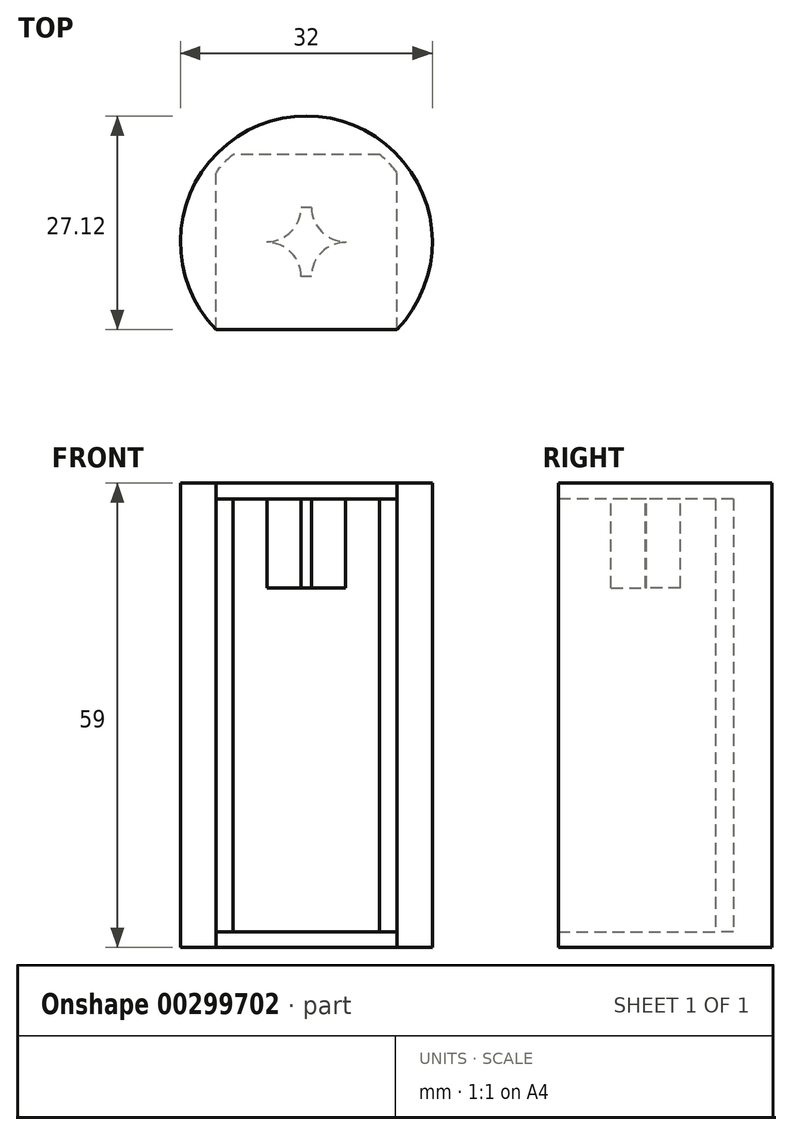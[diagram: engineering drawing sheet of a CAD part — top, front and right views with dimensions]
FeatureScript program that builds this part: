
annotation { "Feature Type Name" : "Feature", "Feature Type Description" : "" }
export const myFeature = defineFeature(function(context is Context, id is Id, definition is map)
    precondition{}
    {
        {
            var Q0;
            Q0=qCreatedBy(makeId("Top.planeOp"),FACE);
            var sketch = newSketch(context, id + "F0", { "sketchPlane" : qUnion([Q0])});
            skCircle(sketch, "E0", {"center": v(0, 0) * mm, "radius": 16 * mm});
            skCircle(sketch, "E1", {"center": v(0, 0) * mm, "radius": 14.5 * mm});
            skSolve(sketch);
        }
        {
            var Q0;
            Q0 = qSketchRegion(id + "F0", true);
            extrude(context, id + "F1", {"entities" : qUnion([Q0]), "depth" : 55 * mm});
        }
        {
            var Q0;
            Q0=makeQuery(id+"F1.opExtrude","CAP_FACE",FACE,{"disambiguationData":[OSD([sQuery(id+"F0.wireOp",EDGE,"E0"),sQuery(id+"F0.wireOp",EDGE,"E1")])],"isStart":false});
            var sketch = newSketch(context, id + "F2", { "sketchPlane" : qUnion([Q0])});
            skCircle(sketch, "E2", {"center": v(0, 0) * mm, "radius": 16 * mm});
            skSolve(sketch);
        }
        {
            var Q0;
            Q0 = qSketchRegion(id + "F2", true);
            extrude(context, id + "F3", {"entities" : qUnion([Q0]), "operationType" : NewBodyOperationType.ADD, "depth" : 2 * mm});
        }
        {
            var Q0;
            Q0=makeQuery(id+"F1.opExtrude","CAP_FACE",FACE,{"disambiguationData":[OSD([sQuery(id+"F0.wireOp",EDGE,"E0"),sQuery(id+"F0.wireOp",EDGE,"E1")])],"isStart":true});
            var sketch = newSketch(context, id + "F4", { "sketchPlane" : qUnion([Q0])});
            skCircle(sketch, "E3", {"center": v(0, 0) * mm, "radius": 16 * mm});
            skSolve(sketch);
        }
        {
            var Q0;
            Q0 = qSketchRegion(id + "F4", true);
            extrude(context, id + "F5", {"entities" : qUnion([Q0]), "operationType" : NewBodyOperationType.ADD, "depth" : 2 * mm});
        }
        {
            var Q0;
            Q0=makeQuery(id+"F5.opExtrude","CAP_FACE",FACE,{"disambiguationData":[OSD([sQuery(id+"F4.wireOp",EDGE,"E3")])],"isStart":false});
            var sketch = newSketch(context, id + "F6", { "sketchPlane" : qUnion([Q0])});
            skLineSegment(sketch, "E4.bottom", {"start": v(11.5, -11.12) * mm, "end": v(-11.5, -11.12) * mm});
            skLineSegment(sketch, "E4.top", {"start": v(11.5, 11.12) * mm, "end": v(-11.5, 11.12) * mm});
            skLineSegment(sketch, "E4.left", {"start": v(11.5, -11.12) * mm, "end": v(11.5, 11.12) * mm});
            skLineSegment(sketch, "E4.right", {"start": v(-11.5, -11.12) * mm, "end": v(-11.5, 11.12) * mm});
            skPoint(sketch, "E4.middle", {"position": v(0, 0) * mm});
            skSolve(sketch);
        }
        {
            var Q0;
            {var subQ0=sQuery(id+"F6.wireOp",EDGE,"E4.top");Q0=makeQuery(id+"F6.imprint","IMPRINT",FACE,{"disambiguationData":[TD([[makeQuery(id+"F6.imprint","IMPRINT",EDGE,{"derivedFrom":subQ0}),-1.0]])]});}
            extrude(context, id + "F7", {"entities" : qUnion([Q0]), "operationType" : NewBodyOperationType.REMOVE, "endBound" : BoundingType.THROUGH_ALL, "oppositeDirection" : true, "depth" : 25 * mm});
        }
        {
            var Q0;
            Q0=makeQuery(id+"F5.opExtrude","CAP_FACE",FACE,{"disambiguationData":[OSD([sQuery(id+"F4.wireOp",EDGE,"E3")])],"isStart":false});
            var sketch = newSketch(context, id + "F8", { "sketchPlane" : qUnion([Q0])});
            skLineSegment(sketch, "E5.bottom", {"start": v(11.5, 11.12) * mm, "end": v(-11.5, 11.12) * mm});
            skLineSegment(sketch, "E5.top", {"start": v(11.5, -11.12) * mm, "end": v(-11.5, -11.12) * mm});
            skLineSegment(sketch, "E5.left", {"start": v(11.5, 11.12) * mm, "end": v(11.5, -11.12) * mm});
            skLineSegment(sketch, "E5.right", {"start": v(-11.5, 11.12) * mm, "end": v(-11.5, -11.12) * mm});
            skPoint(sketch, "E5.middle", {"position": v(0, 0) * mm});
            skSolve(sketch);
        }
        {
            var Q0;
            {var subQ0=sQuery(id+"F8.wireOp",EDGE,"E5.right");Q0=makeQuery(id+"F8.imprint","IMPRINT",FACE,{"disambiguationData":[TD([[makeQuery(id+"F8.imprint","IMPRINT",EDGE,{"derivedFrom":subQ0}),-1.0]])]});}
            var Q1;
            {var subQ0=sQuery(id+"F8.wireOp",EDGE,"E5.top");Q1=makeQuery(id+"F8.imprint","IMPRINT",FACE,{"disambiguationData":[TD([[makeQuery(id+"F8.imprint","IMPRINT",EDGE,{"derivedFrom":subQ0}),1.0]])]});}
            var Q2;
            {var subQ0=sQuery(id+"F8.wireOp",EDGE,"E5.left");Q2=makeQuery(id+"F8.imprint","IMPRINT",FACE,{"disambiguationData":[TD([[makeQuery(id+"F8.imprint","IMPRINT",EDGE,{"derivedFrom":subQ0}),1.0]])]});}
            extrude(context, id + "F9", {"entities" : qUnion([Q0, Q1, Q2]), "operationType" : NewBodyOperationType.ADD, "oppositeDirection" : true, "depth" : 58 * mm});
        }
        {
            var Q0;
            Q0=makeQuery(id+"F7.boolean.opBoolean","COPY",FACE,{"derivedFrom":makeQuery(id+"F7.opExtrude","SWEPT_FACE",FACE,{"disambiguationData":[OSD([sQuery(id+"F6.wireOp",EDGE,"E4.top")])]})});
            var sketch = newSketch(context, id + "F10", { "sketchPlane" : qUnion([Q0])});
            skLineSegment(sketch, "E6.bottom", {"start": v(-11.5, 0) * mm, "end": v(11.5, 0) * mm});
            skLineSegment(sketch, "E6.top", {"start": v(-11.5, 55) * mm, "end": v(11.5, 55) * mm});
            skLineSegment(sketch, "E6.left", {"start": v(-11.5, 0) * mm, "end": v(-11.5, 55) * mm});
            skLineSegment(sketch, "E6.right", {"start": v(11.5, 0) * mm, "end": v(11.5, 55) * mm});
            skSolve(sketch);
        }
        {
            var Q0;
            Q0 = qSketchRegion(id + "F10", true);
            extrude(context, id + "F11", {"entities" : qUnion([Q0]), "operationType" : NewBodyOperationType.REMOVE, "oppositeDirection" : true, "depth" : 3 * mm});
        }
        {
            var Q0;
            Q0=makeQuery(id+"F11.boolean.opBoolean","MERGE",FACE,{"derivedFrom":[makeQuery(id+"F3.opExtrude","CAP_FACE",FACE,{"disambiguationData":[OSD([sQuery(id+"F2.wireOp",EDGE,"E2")])],"isStart":true}),makeQuery(id+"F11.opExtrude","SWEPT_FACE",FACE,{"disambiguationData":[OSD([sQuery(id+"F10.wireOp",EDGE,"E6.top")])]})]});
            var sketch = newSketch(context, id + "F12", { "sketchPlane" : qUnion([Q0])});
            skLineSegment(sketch, "E7.bottom", {"start": v(5, -4.4) * mm, "end": v(-5, -4.4) * mm});
            skLineSegment(sketch, "E7.top", {"start": v(5, 4.4) * mm, "end": v(-5, 4.4) * mm});
            skLineSegment(sketch, "E7.left", {"start": v(5, -4.4) * mm, "end": v(5, 4.4) * mm});
            skLineSegment(sketch, "E7.right", {"start": v(-5, -4.4) * mm, "end": v(-5, 4.4) * mm});
            skPoint(sketch, "E7.middle", {"position": v(0, 0) * mm});
            skCircle(sketch, "E8", {"center": v(5, 4.4) * mm, "radius": 4.35 * mm});
            skCircle(sketch, "E9", {"center": v(-5, 4.4) * mm, "radius": 4.35 * mm});
            skCircle(sketch, "E10", {"center": v(-5, -4.4) * mm, "radius": 4.35 * mm});
            skCircle(sketch, "E11", {"center": v(5, -4.4) * mm, "radius": 4.35 * mm});
            skSolve(sketch);
        }
        {
            var Q0;
            Q0=makeQuery(id+"F12.imprint","IMPRINT",FACE,{"disambiguationData":[TD([[makeQuery(id+"F12.imprint","IMPRINT",EDGE,{"derivedFrom":makeQuery(id+"F1.opExtrude","CAP_EDGE",EDGE,{"disambiguationData":[OSD([sQuery(id+"F0.wireOp",EDGE,"E1")])],"isStart":false})}),-1.0]])]});
            var Q1;
            {var subQ5=sQuery(id+"F12.wireOp",EDGE,"E11");var subQ10=sQuery(id+"F12.wireOp",EDGE,"E7.bottom");var subQ11=makeQuery(id+"F12.imprint","INTERSECT",VERTEX,{"derivedFrom":[subQ10,subQ5]});Q1=makeQuery(id+"F12.imprint","IMPRINT",FACE,{"disambiguationData":[TD([[makeQuery(id+"F12.imprint","IMPRINT",EDGE,{"disambiguationData":[TD([[subQ11,-1.0]])],"derivedFrom":subQ10}),-1.0]])]});}
            extrude(context, id + "F13", {"entities" : qUnion([Q0, Q1]), "operationType" : NewBodyOperationType.ADD, "depth" : 11.3 * mm});
        }
    });
